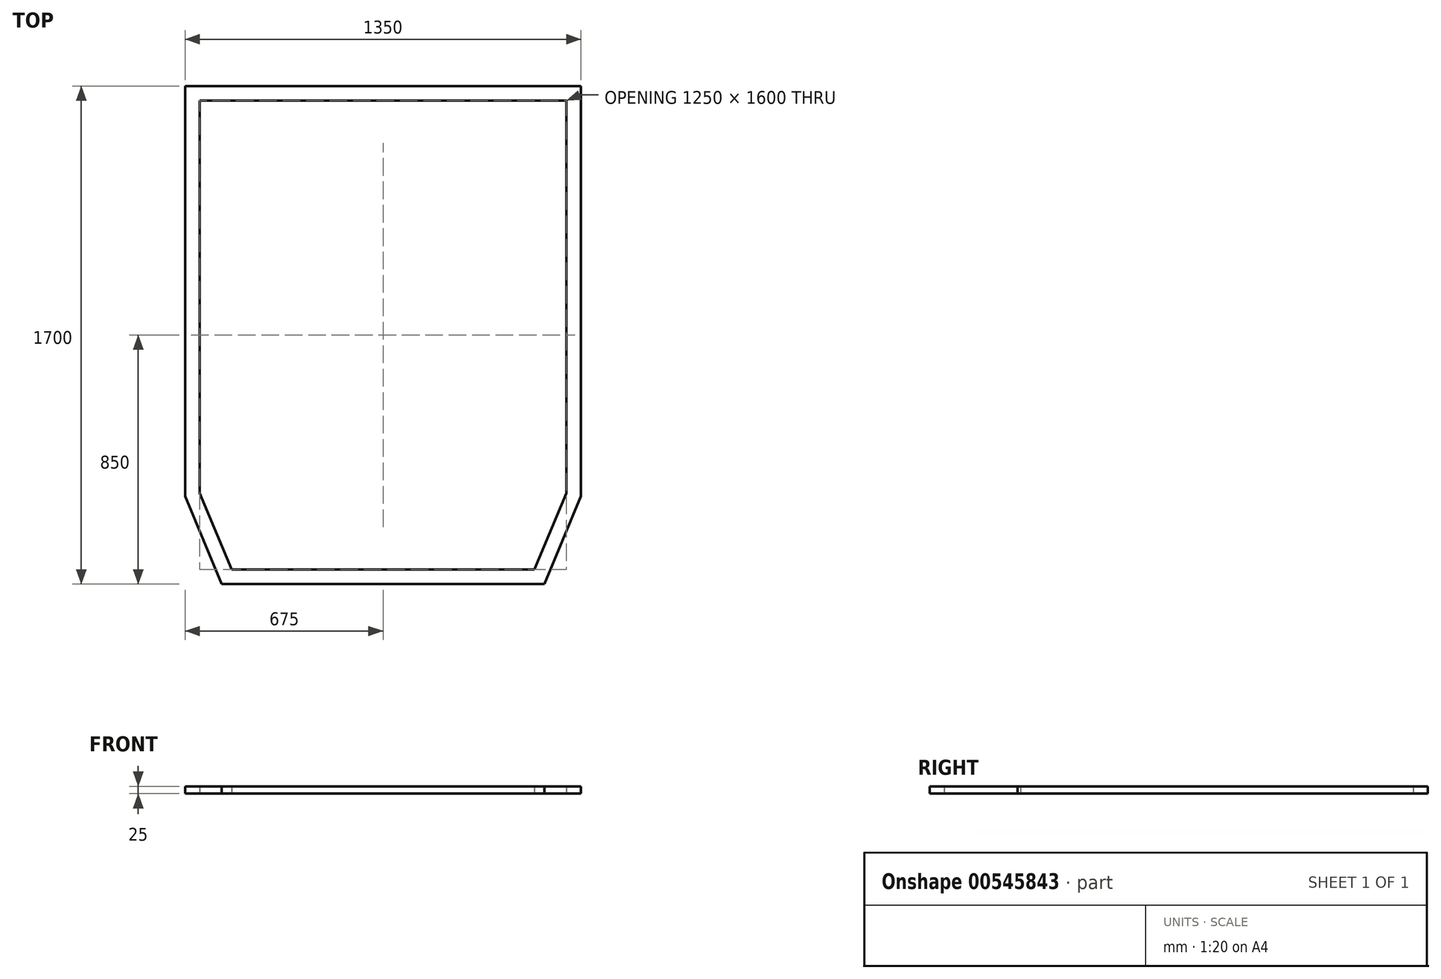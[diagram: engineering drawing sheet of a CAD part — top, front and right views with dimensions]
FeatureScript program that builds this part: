
annotation { "Feature Type Name" : "Feature", "Feature Type Description" : "" }
export const myFeature = defineFeature(function(context is Context, id is Id, definition is map)
    precondition{}
    {
        {
            var Q0;
            Q0=qCreatedBy(makeId("Top.planeOp"),FACE);
            var sketch = newSketch(context, id + "F0", { "sketchPlane" : qUnion([Q0])});
            skLineSegment(sketch, "E0", {"start": v(0, 850) * mm, "end": v(0, -850) * mm, "construction": true});
            skLineSegment(sketch, "E1", {"start": v(0, -850) * mm, "end": v(-550, -850) * mm});
            skLineSegment(sketch, "E2", {"start": v(-550, -850) * mm, "end": v(-675, -550) * mm});
            skLineSegment(sketch, "E3", {"start": v(-675, -550) * mm, "end": v(-675, 850) * mm});
            skLineSegment(sketch, "E4", {"start": v(-675, 850) * mm, "end": v(0, 850) * mm});
            skLineSegment(sketch, "E5", {"start": v(-675, -550) * mm, "end": v(-675, -850) * mm, "construction": true});
            skLineSegment(sketch, "E6", {"start": v(-675, -850) * mm, "end": v(-550, -850) * mm, "construction": true});
            skLineSegment(sketch, "E7.MirrorCS", {"start": v(675, 850) * mm, "end": v(0, 850) * mm});
            skLineSegment(sketch, "E8.MirrorCS", {"start": v(675, -550) * mm, "end": v(675, 850) * mm});
            skLineSegment(sketch, "E9.MirrorCS", {"start": v(550, -850) * mm, "end": v(675, -550) * mm});
            skLineSegment(sketch, "E10.MirrorCS", {"start": v(0, -850) * mm, "end": v(550, -850) * mm});
            skLineSegment(sketch, "E11.0", {"start": v(-516.67, -800) * mm, "end": v(-625, -540) * mm});
            skLineSegment(sketch, "E11.1", {"start": v(0, -800) * mm, "end": v(-516.67, -800) * mm});
            skLineSegment(sketch, "E11.2", {"start": v(-625, -540) * mm, "end": v(-625, 800) * mm});
            skLineSegment(sketch, "E11.3", {"start": v(0, -800) * mm, "end": v(516.67, -800) * mm});
            skLineSegment(sketch, "E11.4", {"start": v(-625, 800) * mm, "end": v(0, 800) * mm});
            skLineSegment(sketch, "E11.5", {"start": v(625, 800) * mm, "end": v(0, 800) * mm});
            skLineSegment(sketch, "E11.6", {"start": v(625, -540) * mm, "end": v(625, 800) * mm});
            skLineSegment(sketch, "E11.7", {"start": v(516.67, -800) * mm, "end": v(625, -540) * mm});
            skSolve(sketch);
        }
        {
            var Q0;
            Q0=makeQuery(id+"F0.imprint","IMPRINT",FACE,{"disambiguationData":[TD([[makeQuery(id+"F0.imprint","IMPRINT",EDGE,{"derivedFrom":sQuery(id+"F0.wireOp",EDGE,"E1")}),-1.0]])]});
            extrude(context, id + "F1", {"entities" : qUnion([Q0]), "endBound" : BoundingType.SYMMETRIC, "depth" : 25 * mm, "offsetDistance" : 25 * mm});
        }
    });
